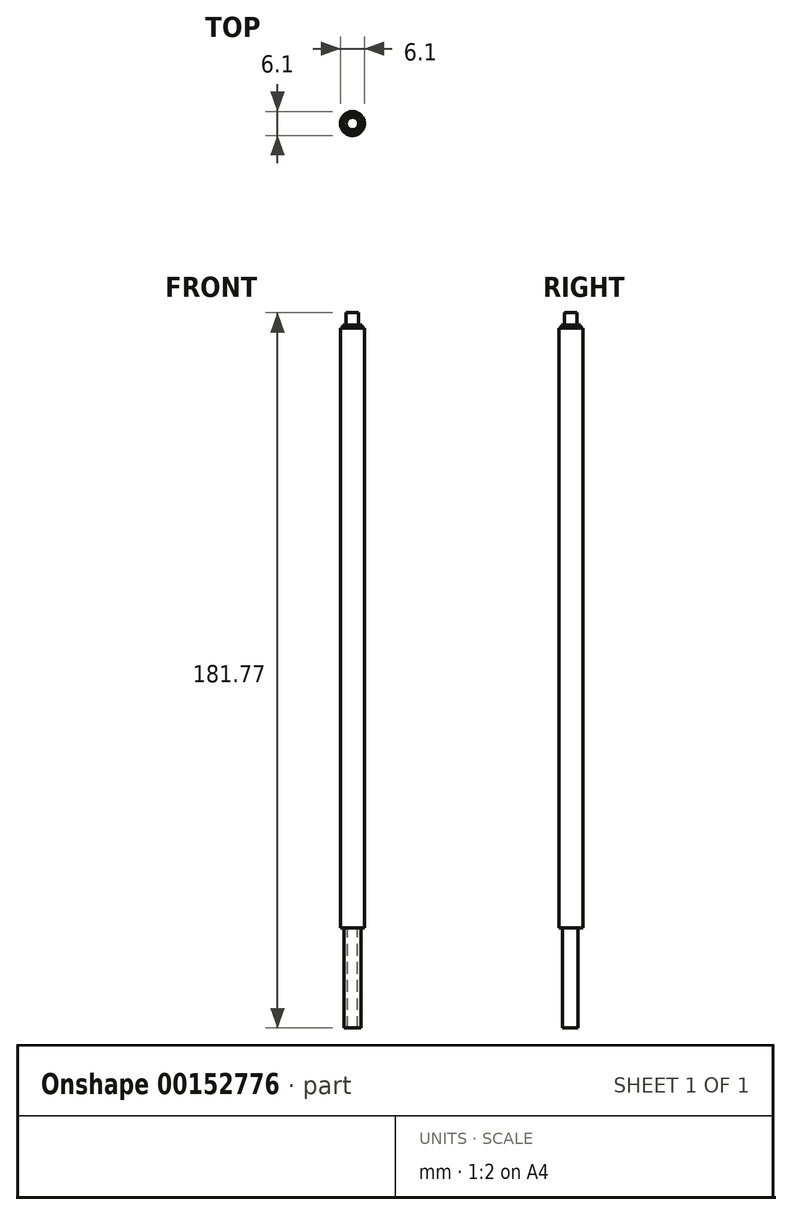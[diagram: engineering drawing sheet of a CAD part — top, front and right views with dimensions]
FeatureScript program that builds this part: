
annotation { "Feature Type Name" : "Feature", "Feature Type Description" : "" }
export const myFeature = defineFeature(function(context is Context, id is Id, definition is map)
    precondition{}
    {
        {
            var Q0;
            Q0=qCreatedBy(makeId("Top.planeOp"),FACE);
            var sketch = newSketch(context, id + "F0", { "sketchPlane" : qUnion([Q0])});
            skCircle(sketch, "E0", {"center": v(0, 0) * mm, "radius": 3.05 * mm});
            skSolve(sketch);
        }
        {
            var Q0;
            Q0 = qSketchRegion(id + "F0", true);
            extrude(context, id + "F1", {"entities" : qUnion([Q0]), "depth" : 152.4 * mm});
        }
        {
            var Q0;
            Q0=makeQuery(id+"F1.opExtrude","CAP_FACE",FACE,{"disambiguationData":[OSD([sQuery(id+"F0.wireOp",EDGE,"E0")])],"isStart":false});
            var sketch = newSketch(context, id + "F2", { "sketchPlane" : qUnion([Q0])});
            skCircle(sketch, "E1", {"center": v(0, 0) * mm, "radius": 2.38 * mm});
            skSolve(sketch);
        }
        {
            var Q0;
            Q0 = qSketchRegion(id + "F2", true);
            extrude(context, id + "F3", {"entities" : qUnion([Q0]), "operationType" : NewBodyOperationType.ADD, "depth" : 0.8 * mm});
        }
        {
            var Q0;
            Q0=makeQuery(id+"F3.opExtrude","CAP_FACE",FACE,{"disambiguationData":[OSD([sQuery(id+"F2.wireOp",EDGE,"E1")])],"isStart":false});
            var sketch = newSketch(context, id + "F4", { "sketchPlane" : qUnion([Q0])});
            skCircle(sketch, "E2", {"center": v(0, 0) * mm, "radius": 1.59 * mm});
            skSolve(sketch);
        }
        {
            var Q0;
            Q0 = qSketchRegion(id + "F4", true);
            extrude(context, id + "F5", {"entities" : qUnion([Q0]), "operationType" : NewBodyOperationType.ADD, "depth" : 3.17 * mm});
        }
        {
            var Q0;
            Q0=makeQuery(id+"F1.opExtrude","CAP_FACE",FACE,{"disambiguationData":[OSD([sQuery(id+"F0.wireOp",EDGE,"E0")])],"isStart":true});
            var sketch = newSketch(context, id + "F6", { "sketchPlane" : qUnion([Q0])});
            skArc(sketch, "E3", {"start": v(1.25, -1.76) * mm, "mid": v(0, 2.15) * mm, "end": v(-1.25, -1.76) * mm});
            skLineSegment(sketch, "E4", {"start": v(0, 0) * mm, "end": v(0, -1.76) * mm, "construction": true});
            skLineSegment(sketch, "E5", {"start": v(0, -1.76) * mm, "end": v(0, -2.15) * mm, "construction": true});
            skArc(sketch, "E6", {"start": v(-1.25, -1.76) * mm, "mid": v(0, -2.15) * mm, "end": v(1.25, -1.76) * mm, "construction": true});
            skLineSegment(sketch, "E7", {"start": v(-1.25, -1.76) * mm, "end": v(1.25, -1.76) * mm});
            skSolve(sketch);
        }
        {
            var Q0;
            Q0 = qSketchRegion(id + "F6", true);
            extrude(context, id + "F7", {"entities" : qUnion([Q0]), "operationType" : NewBodyOperationType.ADD, "depth" : 25.4 * mm});
        }
    });
